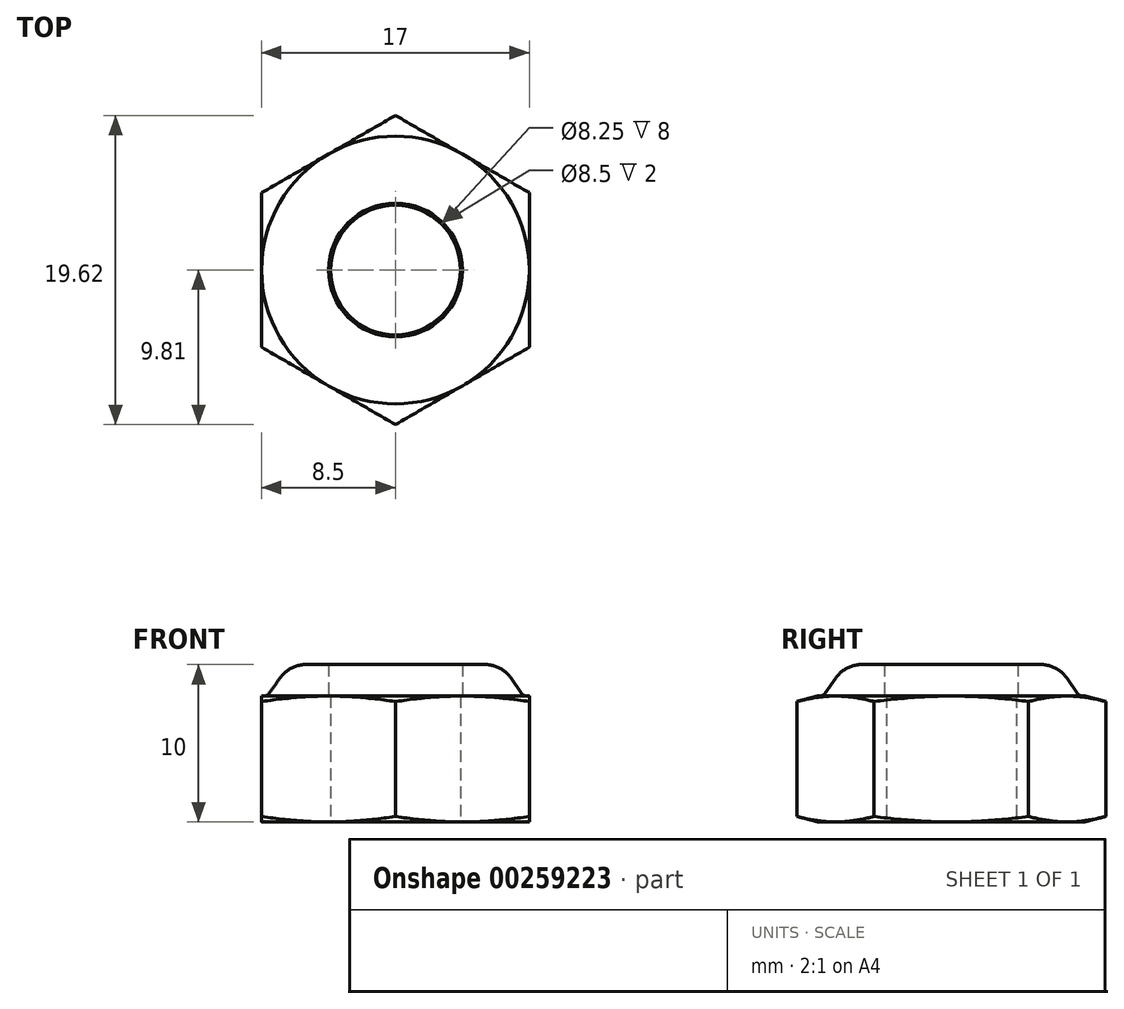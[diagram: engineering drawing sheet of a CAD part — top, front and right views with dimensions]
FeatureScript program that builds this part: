
annotation { "Feature Type Name" : "Feature", "Feature Type Description" : "" }
export const myFeature = defineFeature(function(context is Context, id is Id, definition is map)
    precondition{}
    {
        {
            var Q0;
            Q0=qCreatedBy(makeId("Top.planeOp"),FACE);
            var sketch = newSketch(context, id + "F0", { "sketchPlane" : qUnion([Q0])});
            skCircle(sketch, "E0.cCircle", {"center": v(0, 0) * mm, "radius": 8.5 * mm, "construction": true});
            skLineSegment(sketch, "E0.0", {"start": v(8.5, 4.9) * mm, "end": v(8.5, -4.9) * mm});
            skLineSegment(sketch, "E0.1", {"start": v(8.5, -4.9) * mm, "end": v(0, -9.81) * mm});
            skLineSegment(sketch, "E0.2", {"start": v(0, -9.81) * mm, "end": v(-8.5, -4.9) * mm});
            skLineSegment(sketch, "E0.3", {"start": v(-8.5, -4.9) * mm, "end": v(-8.5, 4.9) * mm});
            skLineSegment(sketch, "E0.4", {"start": v(-8.5, 4.9) * mm, "end": v(0, 9.81) * mm});
            skLineSegment(sketch, "E0.5", {"start": v(0, 9.81) * mm, "end": v(8.5, 4.9) * mm});
            skPoint(sketch, "E0.0.midPoint", {"position": v(8.5, 0) * mm});
            skCircle(sketch, "E1", {"center": v(0, 0) * mm, "radius": 4.12 * mm});
            skLineSegment(sketch, "E2", {"start": v(-12.53, -7.23) * mm, "end": v(14.01, 8.09) * mm, "construction": true});
            skPoint(sketch, "E3", {"position": v(-7.36, -4.25) * mm});
            skPoint(sketch, "E4", {"position": v(-8.5, -4.9) * mm});
            skSolve(sketch);
        }
        {
            var Q0;
            Q0=qSketchRegion(id+"F0",true);
            extrude(context, id + "F1", {"entities" : qUnion([Q0]), "depth" : 8 * mm});
        }
        {
            var Q0;
            Q0=makeQuery(id+"F1.opExtrude","SWEPT_EDGE",EDGE,{"disambiguationData":[OSD([sQuery(id+"F0.wireOp",EDGE,"E0.2"),sQuery(id+"F0.wireOp",EDGE,"E0.3")])]});
            cPoint(context, id + "F2", {"entities" : qUnion([Q0]), "parameter" : 0.5});
        }
        {
            var Q0;
            Q0=makeQuery(id+"F1.opExtrude","SWEPT_EDGE",EDGE,{"disambiguationData":[OSD([sQuery(id+"F0.wireOp",EDGE,"E0.0"),sQuery(id+"F0.wireOp",EDGE,"E0.5")])]});
            cPoint(context, id + "F3", {"entities" : qUnion([Q0]), "parameter" : 0.5});
        }
        {
            var Q0;
            Q0=qCreatedBy(id+"F2",VERTEX);
            var Q1;
            Q1=qCreatedBy(id+"F3",VERTEX);
            var Q2;
            Q2=makeQuery(id+"F1.opExtrude","CAP_VERTEX",VERTEX,{"disambiguationData":[OSD([sQuery(id+"F0.wireOp",EDGE,"E0.0"),sQuery(id+"F0.wireOp",EDGE,"E0.5")])],"isStart":true});
            cPlane(context, id + "F4", {"entities" : qUnion([Q0, Q1, Q2]), "cplaneType" : CPlaneType.THREE_POINT, "offset" : 25 * mm, "width" : 150 * mm, "height" : 150 * mm});
        }
        {
            var Q0;
            Q0=qCreatedBy(id+"F4.planeOp",FACE);
            var sketch = newSketch(context, id + "F5", { "sketchPlane" : qUnion([Q0])});
            skPoint(sketch, "E5.0", {"position": v(-8.5, 0) * mm});
            skLineSegment(sketch, "E6", {"start": v(-2.9, -1.5) * mm, "end": v(-15.32, 1.83) * mm});
            skPoint(sketch, "E7", {"position": v(-9.81, 8) * mm});
            skPoint(sketch, "E8", {"position": v(-9.81, 4) * mm});
            skLineSegment(sketch, "E9", {"start": v(-13.9, 4) * mm, "end": v(7.47, 4) * mm, "construction": true});
            skLineSegment(sketch, "E10", {"start": v(-15.32, -1.5) * mm, "end": v(-2.9, -1.5) * mm});
            skLineSegment(sketch, "E11", {"start": v(0, -0.96) * mm, "end": v(0, 9.49) * mm, "construction": true});
            skPoint(sketch, "E12.trimOffspring.end.orphan", {"position": v(-9.81, 0) * mm});
            skLineSegment(sketch, "E13", {"start": v(-15.32, 1.83) * mm, "end": v(-15.32, -1.5) * mm});
            skPoint(sketch, "E14.end.orphan", {"position": v(-10.64, -1.5) * mm});
            skPoint(sketch, "E14.start.orphan", {"position": v(-10.64, 0.57) * mm});
            skPoint(sketch, "E15.MirrorCS.start.orphan", {"position": v(-10.64, 7.43) * mm});
            skLineSegment(sketch, "E16.MirrorCS", {"start": v(-15.32, 6.17) * mm, "end": v(-15.32, 9.5) * mm});
            skLineSegment(sketch, "E17.MirrorCS", {"start": v(-2.9, 9.5) * mm, "end": v(-15.32, 6.17) * mm});
            skLineSegment(sketch, "E18.MirrorCS", {"start": v(-15.32, 9.5) * mm, "end": v(-2.9, 9.5) * mm});
            skPoint(sketch, "E19.MirrorP", {"position": v(-8.5, 8) * mm});
            skSolve(sketch);
        }
        {
            var Q0;
            Q0=makeQuery(id+"F5.imprint","IMPRINT",FACE,{"disambiguationData":[TD([[makeQuery(id+"F5.imprint","IMPRINT",EDGE,{"derivedFrom":sQuery(id+"F5.wireOp",EDGE,"E16.MirrorCS")}),-1.0]])]});
            var Q1;
            Q1=makeQuery(id+"F5.imprint","IMPRINT",FACE,{"disambiguationData":[TD([[makeQuery(id+"F5.imprint","IMPRINT",EDGE,{"derivedFrom":sQuery(id+"F5.wireOp",EDGE,"E6")}),1.0]])]});
            var Q2;
            Q2=sQuery(id+"F5.wireOp",EDGE,"E11");
            revolve(context, id + "F6", {"operationType" : NewBodyOperationType.REMOVE, "entities" : qUnion([Q0, Q1]), "axis" : qUnion([Q2]), "revolveType" : RevolveType.FULL, "oppositeDirection" : true});
        }
        {
            var Q0;
            Q0=qCreatedBy(makeId("Front.planeOp"),FACE);
            var sketch = newSketch(context, id + "F7", { "sketchPlane" : qUnion([Q0])});
            skLineSegment(sketch, "E20", {"start": v(-4.25, 8) * mm, "end": v(-4.25, 10) * mm});
            skLineSegment(sketch, "E21", {"start": v(-4.25, 8) * mm, "end": v(-8.34, 8) * mm});
            skLineSegment(sketch, "E22.0", {"start": v(-8.5, 8) * mm, "end": v(-8.34, 8) * mm});
            skLineSegment(sketch, "E23", {"start": v(-7.33, 9.15) * mm, "end": v(-8.01, 8.17) * mm});
            skArc(sketch, "E24.filletArc", {"start": v(-8.34, 8) * mm, "mid": v(-8.16, 8.05) * mm, "end": v(-8.01, 8.17) * mm});
            skLineSegment(sketch, "E25", {"start": v(-4.25, 10) * mm, "end": v(-5.7, 10) * mm});
            skArc(sketch, "E26.filletArc", {"start": v(-5.7, 10) * mm, "mid": v(-6.62, 9.77) * mm, "end": v(-7.33, 9.15) * mm});
            skSolve(sketch);
        }
        {
            var Q0;
            Q0=qSketchRegion(id+"F7",true);
            var Q1;
            Q1=sQuery(id+"F5.wireOp",EDGE,"E11");
            revolve(context, id + "F8", {"operationType" : NewBodyOperationType.ADD, "entities" : qUnion([Q0]), "axis" : qUnion([Q1]), "revolveType" : RevolveType.FULL});
        }
    });
